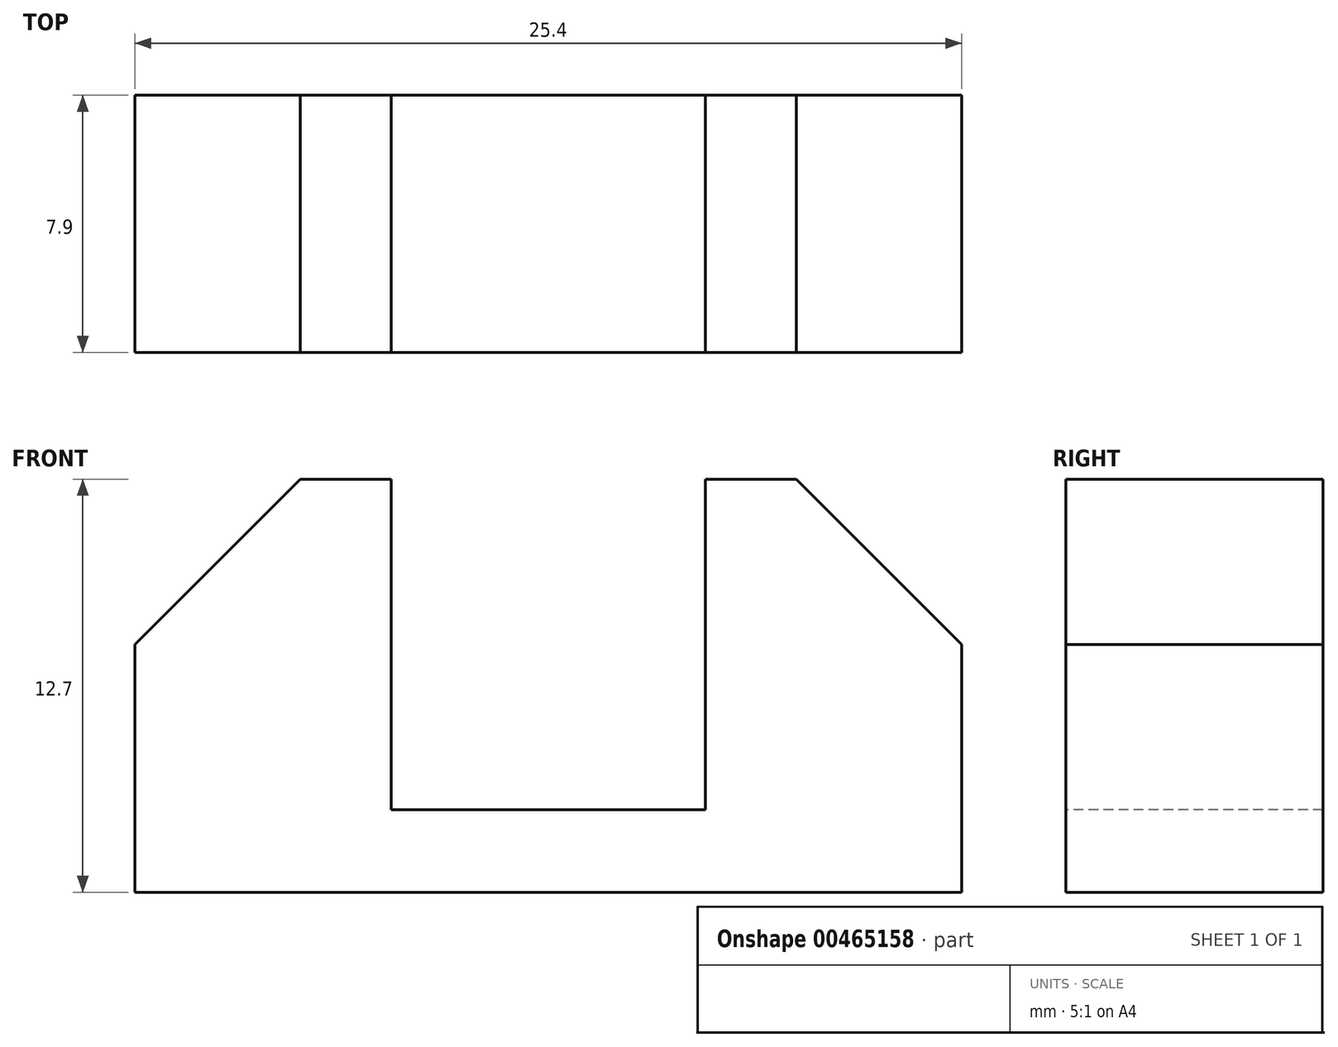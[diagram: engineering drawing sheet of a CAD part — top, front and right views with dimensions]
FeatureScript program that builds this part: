
annotation { "Feature Type Name" : "Feature", "Feature Type Description" : "" }
export const myFeature = defineFeature(function(context is Context, id is Id, definition is map)
    precondition{}
    {
        {
            var Q0;
            Q0=qCreatedBy(makeId("Top.planeOp"),FACE);
            var sketch = newSketch(context, id + "F0", { "sketchPlane" : qUnion([Q0])});
            skLineSegment(sketch, "E0.bottom", {"start": v(-12.7, 3.95) * mm, "end": v(12.7, 3.95) * mm});
            skLineSegment(sketch, "E0.top", {"start": v(-12.7, -3.95) * mm, "end": v(12.7, -3.95) * mm});
            skLineSegment(sketch, "E0.left", {"start": v(-12.7, 3.95) * mm, "end": v(-12.7, -3.95) * mm});
            skLineSegment(sketch, "E0.right", {"start": v(12.7, 3.95) * mm, "end": v(12.7, -3.95) * mm});
            skPoint(sketch, "E0.middle", {"position": v(0, 0) * mm});
            skSolve(sketch);
        }
        {
            var Q0;
            Q0=makeQuery(id+"F0.imprint","IMPRINT",FACE,{"disambiguationData":[TD([[makeQuery(id+"F0.imprint","IMPRINT",EDGE,{"derivedFrom":sQuery(id+"F0.wireOp",EDGE,"E0.bottom")}),-1.0]])]});
            extrude(context, id + "F1", {"entities" : qUnion([Q0]), "depth" : 12.7 * mm});
        }
        {
            var Q0;
            Q0=makeQuery(id+"F1.opExtrude","CAP_EDGE",EDGE,{"disambiguationData":[OSD([sQuery(id+"F0.wireOp",EDGE,"E0.right")])],"isStart":false});
            var Q1;
            Q1=makeQuery(id+"F1.opExtrude","CAP_EDGE",EDGE,{"disambiguationData":[OSD([sQuery(id+"F0.wireOp",EDGE,"E0.left")])],"isStart":false});
            chamfer(context, id + "F2", {"entities" : qUnion([Q0, Q1]), "width" : 5.08 * mm, "tangentPropagation" : true});
        }
        {
            var Q0;
            Q0=makeQuery(id+"F1.opExtrude","CAP_FACE",FACE,{"disambiguationData":[OSD([sQuery(id+"F0.wireOp",EDGE,"E0.bottom"),sQuery(id+"F0.wireOp",EDGE,"E0.top"),sQuery(id+"F0.wireOp",EDGE,"E0.left"),sQuery(id+"F0.wireOp",EDGE,"E0.right")])],"isStart":false});
            var sketch = newSketch(context, id + "F3", { "sketchPlane" : qUnion([Q0])});
            skLineSegment(sketch, "E1", {"start": v(0, -3.95) * mm, "end": v(0, 3.95) * mm, "construction": true});
            skLineSegment(sketch, "E2.bottom", {"start": v(-4.83, 3.95) * mm, "end": v(4.83, 3.95) * mm});
            skLineSegment(sketch, "E2.top", {"start": v(-4.83, -3.95) * mm, "end": v(4.83, -3.95) * mm});
            skLineSegment(sketch, "E2.left", {"start": v(-4.83, 3.95) * mm, "end": v(-4.83, -3.95) * mm});
            skLineSegment(sketch, "E2.right", {"start": v(4.83, 3.95) * mm, "end": v(4.83, -3.95) * mm});
            skPoint(sketch, "E2.middle", {"position": v(0, 0) * mm});
            skSolve(sketch);
        }
        {
            var Q0;
            Q0=makeQuery(id+"F3.imprint","IMPRINT",FACE,{"disambiguationData":[TD([[makeQuery(id+"F3.imprint","IMPRINT",EDGE,{"derivedFrom":sQuery(id+"F3.wireOp",EDGE,"E2.bottom")}),-1.0]])]});
            extrude(context, id + "F4", {"entities" : qUnion([Q0]), "operationType" : NewBodyOperationType.REMOVE, "oppositeDirection" : true, "depth" : 10.16 * mm});
        }
    });
